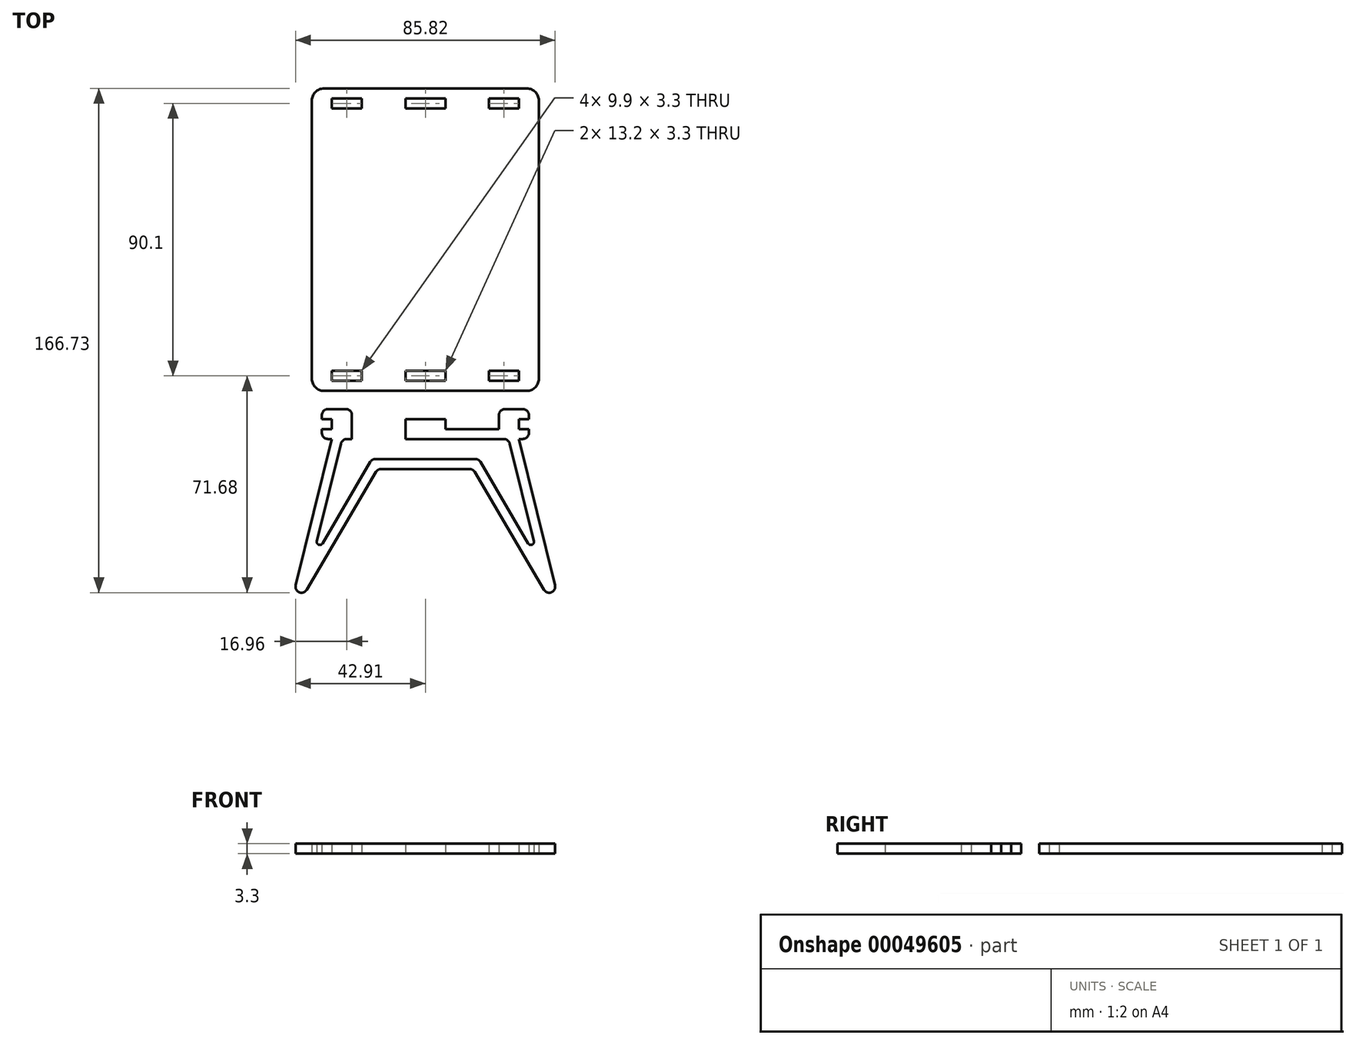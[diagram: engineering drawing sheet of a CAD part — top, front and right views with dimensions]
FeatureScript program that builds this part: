
annotation { "Feature Type Name" : "Feature", "Feature Type Description" : "" }
export const myFeature = defineFeature(function(context is Context, id is Id, definition is map)
    precondition{}
    {
        {
            assignVariable(context, id + "F0", {"name" : "Thickness", "anyValue" : 3.3});
        }
        {
            var Q0;
            Q0=qCreatedBy(makeId("Top.planeOp"),FACE);
            var sketch = newSketch(context, id + "F1", { "sketchPlane" : qUnion([Q0])});
            skLineSegment(sketch, "E0", {"start": v(0, 4) * mm, "end": v(0, 96) * mm});
            skLineSegment(sketch, "E1", {"start": v(4, 100) * mm, "end": v(71, 100) * mm});
            skLineSegment(sketch, "E2", {"start": v(75, 96) * mm, "end": v(75, 4) * mm});
            skLineSegment(sketch, "E3", {"start": v(71, 0) * mm, "end": v(4, 0) * mm});
            skLineSegment(sketch, "E4", {"start": v(37.5, 100) * mm, "end": v(37.5, 0) * mm, "construction": true});
            skLineSegment(sketch, "E5", {"start": v(0, 50) * mm, "end": v(75, 50) * mm, "construction": true});
            skLineSegment(sketch, "E6", {"start": v(6.6, -15.9) * mm, "end": v(-5.35, -64.25) * mm});
            skLineSegment(sketch, "E7", {"start": v(-1.68, -65.75) * mm, "end": v(21.2, -26.79) * mm});
            skLineSegment(sketch, "E8", {"start": v(6.6, -15.9) * mm, "end": v(5.3, -15.9) * mm});
            skLineSegment(sketch, "E9", {"start": v(3.3, -13.9) * mm, "end": v(3.3, -12.6) * mm});
            skLineSegment(sketch, "E10", {"start": v(3.3, -12.6) * mm, "end": v(6.6, -12.6) * mm});
            skLineSegment(sketch, "E11", {"start": v(6.6, -12.6) * mm, "end": v(6.6, -9.3) * mm});
            skLineSegment(sketch, "E12", {"start": v(6.6, -9.3) * mm, "end": v(3.3, -9.3) * mm});
            skLineSegment(sketch, "E13", {"start": v(3.3, -9.3) * mm, "end": v(3.3, -8) * mm});
            skLineSegment(sketch, "E14", {"start": v(5.3, -6) * mm, "end": v(11.2, -6) * mm});
            skLineSegment(sketch, "E15", {"start": v(13.2, -8) * mm, "end": v(13.2, -12.6) * mm});
            skLineSegment(sketch, "E16", {"start": v(19.32, -23.49) * mm, "end": v(3.48, -50.45) * mm});
            skLineSegment(sketch, "E17", {"start": v(1.65, -49.7) * mm, "end": v(9.62, -17.42) * mm});
            skLineSegment(sketch, "E18", {"start": v(11.57, -15.9) * mm, "end": v(13.2, -15.9) * mm});
            skLineSegment(sketch, "E19", {"start": v(30.9, -12.6) * mm, "end": v(30.9, -9.3) * mm});
            skLineSegment(sketch, "E20", {"start": v(37.5, 0) * mm, "end": v(37.5, -56.37) * mm, "construction": true});
            skPoint(sketch, "E21.visualSharp", {"position": v(-8.64, -77.6) * mm});
            skArc(sketch, "E21.filletArc", {"start": v(-5.35, -64.25) * mm, "mid": v(-4.16, -66.59) * mm, "end": v(-1.68, -65.75) * mm});
            skPoint(sketch, "E22.visualSharp", {"position": v(0, -56.37) * mm});
            skArc(sketch, "E22.filletArc", {"start": v(1.65, -49.7) * mm, "mid": v(2.24, -50.87) * mm, "end": v(3.48, -50.45) * mm});
            skLineSegment(sketch, "E23", {"start": v(6.6, 3.3) * mm, "end": v(6.6, 6.6) * mm});
            skLineSegment(sketch, "E24", {"start": v(6.6, 6.6) * mm, "end": v(16.5, 6.6) * mm});
            skLineSegment(sketch, "E25", {"start": v(16.5, 6.6) * mm, "end": v(16.5, 3.3) * mm});
            skLineSegment(sketch, "E26", {"start": v(16.5, 3.3) * mm, "end": v(6.6, 3.3) * mm});
            skLineSegment(sketch, "E27.MirrorCS", {"start": v(58.5, 6.6) * mm, "end": v(58.5, 3.3) * mm});
            skLineSegment(sketch, "E28.MirrorCS", {"start": v(68.4, 6.6) * mm, "end": v(58.5, 6.6) * mm});
            skLineSegment(sketch, "E29.MirrorCS", {"start": v(68.4, 3.3) * mm, "end": v(68.4, 6.6) * mm});
            skLineSegment(sketch, "E30.MirrorCS", {"start": v(58.5, 3.3) * mm, "end": v(68.4, 3.3) * mm});
            skLineSegment(sketch, "E31.MirrorCS", {"start": v(68.4, 96.7) * mm, "end": v(68.4, 93.4) * mm});
            skLineSegment(sketch, "E32.MirrorCS", {"start": v(6.6, 96.7) * mm, "end": v(6.6, 93.4) * mm});
            skLineSegment(sketch, "E33.MirrorCS", {"start": v(16.5, 93.4) * mm, "end": v(16.5, 96.7) * mm});
            skLineSegment(sketch, "E34.MirrorCS", {"start": v(58.5, 93.4) * mm, "end": v(58.5, 96.7) * mm});
            skLineSegment(sketch, "E35.MirrorCS", {"start": v(58.5, 96.7) * mm, "end": v(68.4, 96.7) * mm});
            skLineSegment(sketch, "E36.MirrorCS", {"start": v(16.5, 96.7) * mm, "end": v(6.6, 96.7) * mm});
            skLineSegment(sketch, "E37.MirrorCS", {"start": v(6.6, 93.4) * mm, "end": v(16.5, 93.4) * mm});
            skLineSegment(sketch, "E38.MirrorCS", {"start": v(68.4, 93.4) * mm, "end": v(58.5, 93.4) * mm});
            skLineSegment(sketch, "E39", {"start": v(30.9, 3.3) * mm, "end": v(30.9, 6.6) * mm});
            skLineSegment(sketch, "E40", {"start": v(44.1, 6.6) * mm, "end": v(44.1, 3.3) * mm});
            skLineSegment(sketch, "E41", {"start": v(44.1, 3.3) * mm, "end": v(30.9, 3.3) * mm});
            skPoint(sketch, "E42.visualSharp", {"position": v(3.3, -6) * mm});
            skArc(sketch, "E42.filletArc", {"start": v(5.3, -6) * mm, "mid": v(3.89, -6.59) * mm, "end": v(3.3, -8) * mm});
            skPoint(sketch, "E43.visualSharp", {"position": v(13.2, -6) * mm});
            skArc(sketch, "E43.filletArc", {"start": v(13.2, -8) * mm, "mid": v(12.61, -6.59) * mm, "end": v(11.2, -6) * mm});
            skLineSegment(sketch, "E44", {"start": v(44.1, 6.6) * mm, "end": v(30.9, 6.6) * mm});
            skLineSegment(sketch, "E45.MirrorCS", {"start": v(30.9, 96.7) * mm, "end": v(30.9, 93.4) * mm});
            skLineSegment(sketch, "E46.MirrorCS", {"start": v(44.1, 96.7) * mm, "end": v(30.9, 96.7) * mm});
            skLineSegment(sketch, "E47.MirrorCS", {"start": v(44.1, 93.4) * mm, "end": v(30.9, 93.4) * mm});
            skLineSegment(sketch, "E48.MirrorCS", {"start": v(44.1, 93.4) * mm, "end": v(44.1, 96.7) * mm});
            skPoint(sketch, "E49.visualSharp", {"position": v(0, 0) * mm});
            skArc(sketch, "E49.filletArc", {"start": v(0, 4) * mm, "mid": v(1.17, 1.17) * mm, "end": v(4, 0) * mm});
            skPoint(sketch, "E50.visualSharp", {"position": v(75, 0) * mm});
            skArc(sketch, "E50.filletArc", {"start": v(71, 0) * mm, "mid": v(73.83, 1.17) * mm, "end": v(75, 4) * mm});
            skPoint(sketch, "E51.visualSharp", {"position": v(75, 100) * mm});
            skArc(sketch, "E51.filletArc", {"start": v(75, 96) * mm, "mid": v(73.83, 98.83) * mm, "end": v(71, 100) * mm});
            skPoint(sketch, "E52.visualSharp", {"position": v(0, 100) * mm});
            skArc(sketch, "E52.filletArc", {"start": v(4, 100) * mm, "mid": v(1.17, 98.83) * mm, "end": v(0, 96) * mm});
            skPoint(sketch, "E53.visualSharp", {"position": v(3.3, -15.9) * mm});
            skArc(sketch, "E53.filletArc", {"start": v(3.3, -13.9) * mm, "mid": v(3.89, -15.31) * mm, "end": v(5.3, -15.9) * mm});
            skLineSegment(sketch, "E54", {"start": v(30.9, -9.3) * mm, "end": v(37.5, -9.3) * mm});
            skLineSegment(sketch, "E55", {"start": v(21.04, -22.5) * mm, "end": v(37.5, -22.5) * mm});
            skLineSegment(sketch, "E56", {"start": v(22.93, -25.8) * mm, "end": v(37.5, -25.8) * mm});
            skPoint(sketch, "E57.visualSharp", {"position": v(10, -15.9) * mm});
            skArc(sketch, "E57.filletArc", {"start": v(11.57, -15.9) * mm, "mid": v(10.33, -16.33) * mm, "end": v(9.62, -17.42) * mm});
            skPoint(sketch, "E58.visualSharp", {"position": v(19.9, -22.5) * mm});
            skArc(sketch, "E58.filletArc", {"start": v(21.04, -22.5) * mm, "mid": v(20.05, -22.76) * mm, "end": v(19.32, -23.49) * mm});
            skPoint(sketch, "E59.visualSharp", {"position": v(21.79, -25.8) * mm});
            skArc(sketch, "E59.filletArc", {"start": v(22.93, -25.8) * mm, "mid": v(21.94, -26.06) * mm, "end": v(21.2, -26.79) * mm});
            skLineSegment(sketch, "E60", {"start": v(13.2, -12.6) * mm, "end": v(13.2, -15.9) * mm});
            skLineSegment(sketch, "E61", {"start": v(30.9, -12.6) * mm, "end": v(30.9, -15.9) * mm});
            skArc(sketch, "E62.MirrorCS", {"start": v(71.7, -13.9) * mm, "mid": v(71.11, -15.31) * mm, "end": v(69.7, -15.9) * mm});
            skArc(sketch, "E63.MirrorCS", {"start": v(73.35, -49.7) * mm, "mid": v(72.76, -50.87) * mm, "end": v(71.52, -50.45) * mm});
            skLineSegment(sketch, "E64.MirrorCS", {"start": v(71.7, -13.9) * mm, "end": v(71.7, -12.6) * mm});
            skArc(sketch, "E65.MirrorCS", {"start": v(53.96, -22.5) * mm, "mid": v(54.95, -22.76) * mm, "end": v(55.68, -23.49) * mm});
            skLineSegment(sketch, "E66.MirrorCS", {"start": v(71.7, -9.3) * mm, "end": v(71.7, -8) * mm});
            skLineSegment(sketch, "E67.MirrorCS", {"start": v(68.4, -15.9) * mm, "end": v(69.7, -15.9) * mm});
            skLineSegment(sketch, "E68.MirrorCS", {"start": v(68.4, -9.3) * mm, "end": v(71.7, -9.3) * mm});
            skLineSegment(sketch, "E69.MirrorCS", {"start": v(71.7, -12.6) * mm, "end": v(68.4, -12.6) * mm});
            skArc(sketch, "E70.MirrorCS", {"start": v(52.07, -25.8) * mm, "mid": v(53.06, -26.06) * mm, "end": v(53.8, -26.79) * mm});
            skArc(sketch, "E71.MirrorCS", {"start": v(63.43, -15.9) * mm, "mid": v(64.67, -16.33) * mm, "end": v(65.38, -17.42) * mm});
            skArc(sketch, "E72.MirrorCS", {"start": v(69.7, -6) * mm, "mid": v(71.11, -6.59) * mm, "end": v(71.7, -8) * mm});
            skArc(sketch, "E73.MirrorCS", {"start": v(61.8, -8) * mm, "mid": v(62.39, -6.59) * mm, "end": v(63.8, -6) * mm});
            skPoint(sketch, "E74.MirrorP", {"position": v(53.21, -25.8) * mm});
            skLineSegment(sketch, "E75.MirrorCS", {"start": v(68.4, -12.6) * mm, "end": v(68.4, -9.3) * mm});
            skPoint(sketch, "E76.MirrorP", {"position": v(65, -15.9) * mm});
            skLineSegment(sketch, "E77.MirrorCS", {"start": v(68.4, -15.9) * mm, "end": v(80.35, -64.25) * mm});
            skLineSegment(sketch, "E78.MirrorCS", {"start": v(53.96, -22.5) * mm, "end": v(37.5, -22.5) * mm});
            skPoint(sketch, "E79.MirrorP", {"position": v(71.7, -6) * mm});
            skPoint(sketch, "E80.MirrorP", {"position": v(55.1, -22.5) * mm});
            skLineSegment(sketch, "E81.MirrorCS", {"start": v(55.68, -23.49) * mm, "end": v(71.52, -50.45) * mm});
            skLineSegment(sketch, "E82.MirrorCS", {"start": v(63.43, -15.9) * mm, "end": v(37.5, -15.9) * mm});
            skPoint(sketch, "E83.MirrorP", {"position": v(75, -56.37) * mm});
            skLineSegment(sketch, "E84.MirrorCS", {"start": v(69.7, -6) * mm, "end": v(63.8, -6) * mm});
            skLineSegment(sketch, "E85.MirrorCS", {"start": v(44.1, -12.6) * mm, "end": v(44.1, -9.3) * mm});
            skLineSegment(sketch, "E86.MirrorCS", {"start": v(52.07, -25.8) * mm, "end": v(37.5, -25.8) * mm});
            skArc(sketch, "E87.MirrorCS", {"start": v(80.35, -64.25) * mm, "mid": v(79.16, -66.59) * mm, "end": v(76.68, -65.75) * mm});
            skPoint(sketch, "E88.MirrorP", {"position": v(71.7, -15.9) * mm});
            skLineSegment(sketch, "E89.MirrorCS", {"start": v(73.35, -49.7) * mm, "end": v(65.38, -17.42) * mm});
            skPoint(sketch, "E90.MirrorP", {"position": v(61.8, -6) * mm});
            skLineSegment(sketch, "E91.MirrorCS", {"start": v(61.8, -8) * mm, "end": v(61.8, -12.6) * mm});
            skLineSegment(sketch, "E92.MirrorCS", {"start": v(76.68, -65.75) * mm, "end": v(53.8, -26.79) * mm});
            skLineSegment(sketch, "E93.MirrorCS", {"start": v(44.1, -9.3) * mm, "end": v(37.5, -9.3) * mm});
            skLineSegment(sketch, "E94", {"start": v(44.1, -12.6) * mm, "end": v(61.8, -12.6) * mm});
            skLineSegment(sketch, "E95.trimOffspring", {"start": v(30.9, -15.9) * mm, "end": v(37.5, -15.9) * mm});
            skSolve(sketch);
        }
        {
            var Q0;
            Q0=makeQuery(id+"F1.imprint","IMPRINT",FACE,{"disambiguationData":[TD([[makeQuery(id+"F1.imprint","IMPRINT",EDGE,{"derivedFrom":sQuery(id+"F1.wireOp",EDGE,"E6")}),1.0]])]});
            var Q1;
            Q1=makeQuery(id+"F1.imprint","IMPRINT",FACE,{"disambiguationData":[TD([[makeQuery(id+"F1.imprint","IMPRINT",EDGE,{"derivedFrom":sQuery(id+"F1.wireOp",EDGE,"E0")}),-1.0]])]});
            extrude(context, id + "F2", {"entities" : qUnion([Q0, Q1]), "depth" : (getVariable(context, 'Thickness')) * mm});
        }
    });
